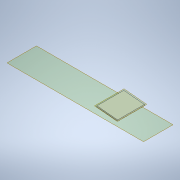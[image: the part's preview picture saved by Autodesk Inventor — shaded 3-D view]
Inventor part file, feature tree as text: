
AUTODESK INVENTOR PART (.ipt)
format: ipt  version: 2020.2 (Build 242310000, 310)  size: 124,928 bytes
history: native  units: mm
features: extrude x3, sketch x3, other x2
ambient origin geometry x8: Origin, YZ Plane, XZ Plane, XY Plane, X Axis, Y Axis, Z Axis, Center Point
bodies: Solide1 (feature_tree)
feature tree (8):
  extrude  "Extrusion1"  Depth=785.7mm
  other  "Plan de construction1"
  extrude  "Extrusion2"  Depth=3.0mm
  other  "Plan de construction2"
  extrude  "Extrusion3"  Depth=14.3mm
  sketch  "Esquisse1"
  sketch  "Esquisse2"
  sketch  "Esquisse3"
